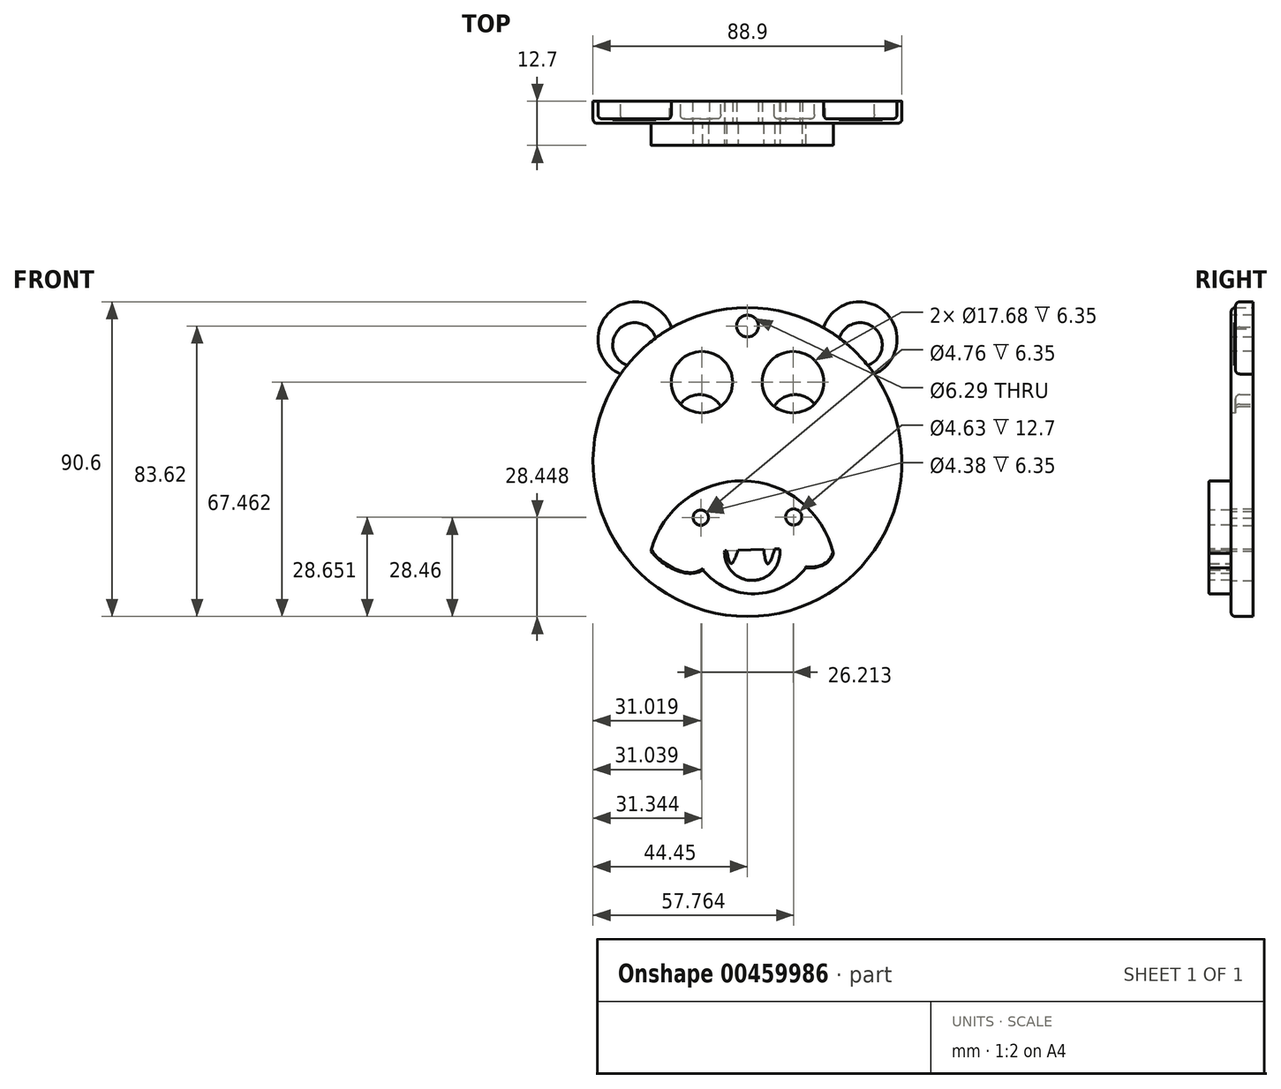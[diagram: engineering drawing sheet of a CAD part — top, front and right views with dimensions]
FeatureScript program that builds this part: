
annotation { "Feature Type Name" : "Feature", "Feature Type Description" : "" }
export const myFeature = defineFeature(function(context is Context, id is Id, definition is map)
    precondition{}
    {
        {
            var Q0;
            Q0=qCreatedBy(makeId("Front.planeOp"),FACE);
            var sketch = newSketch(context, id + "F0", { "sketchPlane" : qUnion([Q0])});
            skCircle(sketch, "E0", {"center": v(0, 0) * mm, "radius": 44.45 * mm});
            skSolve(sketch);
        }
        {
            var Q0;
            Q0 = qSketchRegion(id + "F0", true);
            extrude(context, id + "F1", {"entities" : qUnion([Q0]), "depth" : 6.35 * mm});
        }
        {
            var Q0;
            Q0=makeQuery(id+"F1.opExtrude","CAP_FACE",FACE,{"disambiguationData":[OSD([sQuery(id+"F0.wireOp",EDGE,"E0")])],"isStart":false});
            var sketch = newSketch(context, id + "F2", { "sketchPlane" : qUnion([Q0])});
            skCircle(sketch, "E1", {"center": v(-13.1, 23.01) * mm, "radius": 8.84 * mm});
            skCircle(sketch, "E2.MirrorC", {"center": v(13.1, 23.01) * mm, "radius": 8.84 * mm});
            skArc(sketch, "E3", {"start": v(-6.7, -25.76) * mm, "mid": v(1.7, -34.27) * mm, "end": v(9.45, -25.15) * mm});
            skLineSegment(sketch, "E4", {"start": v(-6.7, -25.76) * mm, "end": v(9.45, -25.15) * mm});
            skCircle(sketch, "E5", {"center": v(-13.41, -16) * mm, "radius": 2.38 * mm});
            skCircle(sketch, "E6.MirrorC", {"center": v(13.41, -16) * mm, "radius": 2.38 * mm});
            skCircle(sketch, "E7", {"center": v(0, 39.17) * mm, "radius": 3.15 * mm});
            skSolve(sketch);
        }
        {
            var Q0;
            Q0 = qSketchRegion(id + "F2", true);
            extrude(context, id + "F3", {"entities" : qUnion([Q0]), "operationType" : NewBodyOperationType.REMOVE, "oppositeDirection" : true, "depth" : 50.8 * mm});
        }
        {
            var Q0;
            Q0=qCreatedBy(makeId("Front.planeOp"),FACE);
            var sketch = newSketch(context, id + "F4", { "sketchPlane" : qUnion([Q0])});
            skArc(sketch, "E8", {"start": v(-21.95, 38.86) * mm, "mid": v(-39.77, 43.06) * mm, "end": v(-35.97, 25.15) * mm});
            skArc(sketch, "E9.MirrorCS", {"start": v(21.95, 38.86) * mm, "mid": v(39.77, 43.06) * mm, "end": v(35.97, 25.15) * mm});
            skLineSegment(sketch, "E10", {"start": v(-35.97, 25.15) * mm, "end": v(-21.95, 38.86) * mm});
            skLineSegment(sketch, "E11", {"start": v(21.95, 38.86) * mm, "end": v(35.97, 25.15) * mm});
            skFitSpline(sketch, "E12", {"points": [v(-6.12, -25.53) * mm, v(-4.46, -29.26) * mm, v(-2.91, -25.22) * mm], "startDerivative": vector(3.5, -9.28) * mm, "endDerivative": vector(3.37, 9.59) * mm});
            skFitSpline(sketch, "E13", {"points": [v(4.45, -24.95) * mm, v(5.46, -29.07) * mm, v(8.02, -24.67) * mm], "startDerivative": vector(1.33, -10.46) * mm, "endDerivative": vector(5.47, 10.16) * mm});
            skFitSpline(sketch, "E14", {"points": [v(-6.12, -25.53) * mm, v(-6.12, -24.67) * mm], "startDerivative": vector(0, 0.57) * mm, "endDerivative": vector(0, 0.57) * mm});
            skLineSegment(sketch, "E15", {"start": v(-6.12, -25.34) * mm, "end": v(-2.91, -25.22) * mm});
            skLineSegment(sketch, "E16", {"start": v(4.45, -24.95) * mm, "end": v(8.02, -24.67) * mm});
            skCircle(sketch, "E17", {"center": v(-13.7, 12.4) * mm, "radius": 7.04 * mm});
            skCircle(sketch, "E18.MirrorC", {"center": v(13.7, 12.4) * mm, "radius": 7.04 * mm});
            skSolve(sketch);
        }
        {
            var Q0;
            Q0 = qSketchRegion(id + "F4", true);
            extrude(context, id + "F5", {"entities" : qUnion([Q0]), "operationType" : NewBodyOperationType.ADD, "depth" : 5.08 * mm});
        }
        {
            var Q0;
            Q0=makeQuery(id+"F1.opExtrude","CAP_FACE",FACE,{"disambiguationData":[OSD([sQuery(id+"F0.wireOp",EDGE,"E0")])],"isStart":false});
            var sketch = newSketch(context, id + "F6", { "sketchPlane" : qUnion([Q0])});
            skArc(sketch, "E19", {"start": v(24.7, -26.27) * mm, "mid": v(-1.25, -5.4) * mm, "end": v(-27.77, -25.54) * mm});
            skFitSpline(sketch, "E20", {"points": [v(-27.77, -25.54) * mm, v(-16.56, -32.05) * mm, v(-6.7, -25.76) * mm], "startDerivative": vector(8.74, -16.07) * mm, "endDerivative": vector(19.75, 19) * mm});
            skFitSpline(sketch, "E21", {"points": [v(9.45, -25.15) * mm, v(16.83, -30.38) * mm, v(24.7, -26.27) * mm], "startDerivative": vector(14.4, -15.09) * mm, "endDerivative": vector(5.4, 20.29) * mm});
            skArc(sketch, "E22", {"start": v(-12.84, -31.06) * mm, "mid": v(2.16, -37.9) * mm, "end": v(16.83, -30.38) * mm});
            skSolve(sketch);
        }
        {
            var Q0;
            Q0 = qSketchRegion(id + "F6", true);
            extrude(context, id + "F7", {"entities" : qUnion([Q0]), "operationType" : NewBodyOperationType.ADD, "depth" : 6.35 * mm});
        }
        {
            var Q0;
            Q0=makeQuery(id+"F7.opExtrude","CAP_FACE",FACE,{"disambiguationData":[OSD([sQuery(id+"F6.wireOp",EDGE,"E19"),sQuery(id+"F6.wireOp",EDGE,"E20"),sQuery(id+"F6.wireOp",EDGE,"E21"),sQuery(id+"F6.wireOp",EDGE,"E22")])],"isStart":false});
            var sketch = newSketch(context, id + "F8", { "sketchPlane" : qUnion([Q0])});
            skCircle(sketch, "E23", {"center": v(-13.43, -15.99) * mm, "radius": 2.2 * mm});
            skCircle(sketch, "E24", {"center": v(13.31, -15.8) * mm, "radius": 2.32 * mm});
            skArc(sketch, "E25", {"start": v(-6.58, -25.5) * mm, "mid": v(1.64, -34.06) * mm, "end": v(9.22, -24.94) * mm});
            skLineSegment(sketch, "E26", {"start": v(-6.58, -25.5) * mm, "end": v(9.22, -24.94) * mm});
            skFitSpline(sketch, "E27", {"points": [v(-6.58, -25.5) * mm, v(-4.58, -29.22) * mm, v(-2.97, -25.38) * mm], "startDerivative": vector(4.17, -11.2) * mm, "endDerivative": vector(3.05, 11.47) * mm});
            skFitSpline(sketch, "E28", {"points": [v(5.13, -25.08) * mm, v(7.03, -29.03) * mm, v(8.37, -24.97) * mm], "startDerivative": vector(4.06, -11.87) * mm, "endDerivative": vector(2.42, 12.15) * mm});
            skSolve(sketch);
        }
        {
            var Q0;
            Q0 = qSketchRegion(id + "F8", true);
            extrude(context, id + "F9", {"entities" : qUnion([Q0]), "operationType" : NewBodyOperationType.REMOVE, "oppositeDirection" : true, "depth" : 25.4 * mm});
        }
        {
            var Q0;
            Q0=makeQuery(id+"F7.opExtrude","CAP_FACE",FACE,{"disambiguationData":[OSD([sQuery(id+"F6.wireOp",EDGE,"E19"),sQuery(id+"F6.wireOp",EDGE,"E20"),sQuery(id+"F6.wireOp",EDGE,"E21"),sQuery(id+"F6.wireOp",EDGE,"E22")])],"isStart":false});
            var sketch = newSketch(context, id + "F10", { "sketchPlane" : qUnion([Q0])});
            skFitSpline(sketch, "E29", {"points": [v(-5.98, -25.49) * mm, v(-4.7, -29.24) * mm, v(-2.73, -25.37) * mm], "startDerivative": vector(2.08, -11.05) * mm, "endDerivative": vector(3.86, 11.35) * mm});
            skFitSpline(sketch, "E30", {"points": [v(4.64, -25.1) * mm, v(5.8, -29.32) * mm, v(7.86, -24.99) * mm], "startDerivative": vector(1.97, -12.8) * mm, "endDerivative": vector(3.25, 12.25) * mm});
            skLineSegment(sketch, "E31", {"start": v(-5.98, -25.49) * mm, "end": v(-2.73, -25.37) * mm});
            skLineSegment(sketch, "E32", {"start": v(4.64, -25.1) * mm, "end": v(7.86, -24.99) * mm});
            skSolve(sketch);
        }
        {
            var Q0;
            Q0=makeQuery(id+"F10.imprint","IMPRINT",FACE,{"disambiguationData":[TD([[makeQuery(id+"F10.imprint","IMPRINT",EDGE,{"derivedFrom":sQuery(id+"F10.wireOp",EDGE,"E29")}),1.0]])]});
            var Q1;
            Q1=makeQuery(id+"F10.imprint","IMPRINT",FACE,{"disambiguationData":[TD([[makeQuery(id+"F10.imprint","IMPRINT",EDGE,{"derivedFrom":sQuery(id+"F10.wireOp",EDGE,"E30")}),1.0]])]});
            extrude(context, id + "F11", {"entities" : qUnion([Q0, Q1]), "operationType" : NewBodyOperationType.ADD, "oppositeDirection" : true, "depth" : 6.35 * mm});
        }
        {
            var Q0;
            Q0=qCreatedBy(makeId("Front.planeOp"),FACE);
            var sketch = newSketch(context, id + "F12", { "sketchPlane" : qUnion([Q0])});
            skArc(sketch, "E33", {"start": v(-26.33, 35.47) * mm, "mid": v(-36.87, 38.33) * mm, "end": v(-34.27, 27.73) * mm});
            skLineSegment(sketch, "E34", {"start": v(-34.27, 27.73) * mm, "end": v(-26.33, 35.47) * mm});
            skArc(sketch, "E35.MirrorCS", {"start": v(26.33, 35.47) * mm, "mid": v(36.87, 38.33) * mm, "end": v(34.27, 27.73) * mm});
            skLineSegment(sketch, "E36.MirrorCS", {"start": v(34.27, 27.73) * mm, "end": v(26.33, 35.47) * mm});
            skSolve(sketch);
        }
        {
            var Q0;
            Q0 = qSketchRegion(id + "F12", true);
            var Q1;
            Q1 = qSketchRegion(id + "F12", true);
            extrude(context, id + "F13", {"entities" : qUnion([Q0, Q1]), "operationType" : NewBodyOperationType.ADD, "depth" : 5.33 * mm});
        }
        {
            var Q0;
            Q0=makeQuery(id+"F1.opExtrude","CAP_EDGE",EDGE,{"disambiguationData":[OSD([sQuery(id+"F0.wireOp",EDGE,"E0")])],"isStart":false});
            var Q1;
            Q1=makeQuery(id+"F3.boolean.opBoolean","COPY",EDGE,{"derivedFrom":makeQuery(id+"F3.opExtrude","CAP_EDGE",EDGE,{"disambiguationData":[OSD([sQuery(id+"F2.wireOp",EDGE,"E1")])],"isStart":true})});
            var Q2;
            Q2=makeQuery(id+"F3.boolean.opBoolean","COPY",EDGE,{"derivedFrom":makeQuery(id+"F3.opExtrude","CAP_EDGE",EDGE,{"disambiguationData":[OSD([sQuery(id+"F2.wireOp",EDGE,"E2.MirrorC")])],"isStart":true})});
            fillet(context, id + "F14", {"entities" : qUnion([Q0, Q1, Q2]), "radius" : 1.27 * mm, "tangentPropagation" : true, "allowEdgeOverflow" : false});
        }
        {
            var Q0;
            Q0=makeQuery(id+"F5.opExtrude","CAP_EDGE",EDGE,{"disambiguationData":[OSD([sQuery(id+"F4.wireOp",EDGE,"E18.MirrorC")])],"isStart":false});
            var Q1;
            Q1=makeQuery(id+"F5.opExtrude","CAP_EDGE",EDGE,{"disambiguationData":[OSD([sQuery(id+"F4.wireOp",EDGE,"E17")])],"isStart":false});
            var Q2;
            Q2=makeQuery(id+"F9.boolean.opBoolean","COPY",EDGE,{"derivedFrom":makeQuery(id+"F9.opExtrude","CAP_EDGE",EDGE,{"disambiguationData":[OSD([sQuery(id+"F8.wireOp",EDGE,"E23")])],"isStart":true})});
            var Q3;
            Q3=makeQuery(id+"F9.boolean.opBoolean","COPY",EDGE,{"derivedFrom":makeQuery(id+"F9.opExtrude","CAP_EDGE",EDGE,{"disambiguationData":[OSD([sQuery(id+"F8.wireOp",EDGE,"E24")])],"isStart":true})});
            fillet(context, id + "F15", {"entities" : qUnion([Q0, Q1, Q2, Q3]), "radius" : 1.27 * mm, "tangentPropagation" : true, "allowEdgeOverflow" : false});
        }
        {
            var Q0;
            Q0=makeQuery(id+"F7.opExtrude","CAP_EDGE",EDGE,{"disambiguationData":[OSD([sQuery(id+"F6.wireOp",EDGE,"E19")])],"isStart":false});
            var Q1;
            Q1=makeQuery(id+"F7.opExtrude","CAP_EDGE",EDGE,{"disambiguationData":[OSD([sQuery(id+"F6.wireOp",EDGE,"E20")])],"isStart":false});
            var Q2;
            Q2=makeQuery(id+"F7.opExtrude","CAP_EDGE",EDGE,{"disambiguationData":[OSD([sQuery(id+"F6.wireOp",EDGE,"E22")])],"isStart":false});
            var Q3;
            Q3=makeQuery(id+"F7.opExtrude","CAP_EDGE",EDGE,{"disambiguationData":[OSD([sQuery(id+"F6.wireOp",EDGE,"E21")])],"isStart":false});
            fillet(context, id + "F16", {"entities" : qUnion([Q0, Q1, Q2, Q3]), "radius" : 0.25 * mm, "tangentPropagation" : true, "allowEdgeOverflow" : false});
        }
        {
            var Q0;
            Q0=makeQuery(id+"F5.opExtrude","CAP_EDGE",EDGE,{"disambiguationData":[OSD([sQuery(id+"F4.wireOp",EDGE,"E8")])],"isStart":false});
            var Q1;
            Q1=makeQuery(id+"F5.opExtrude","CAP_EDGE",EDGE,{"disambiguationData":[OSD([sQuery(id+"F4.wireOp",EDGE,"E9.MirrorCS")])],"isStart":false});
            fillet(context, id + "F17", {"entities" : qUnion([Q0, Q1]), "radius" : 1.27 * mm, "tangentPropagation" : true, "allowEdgeOverflow" : false});
        }
    });
